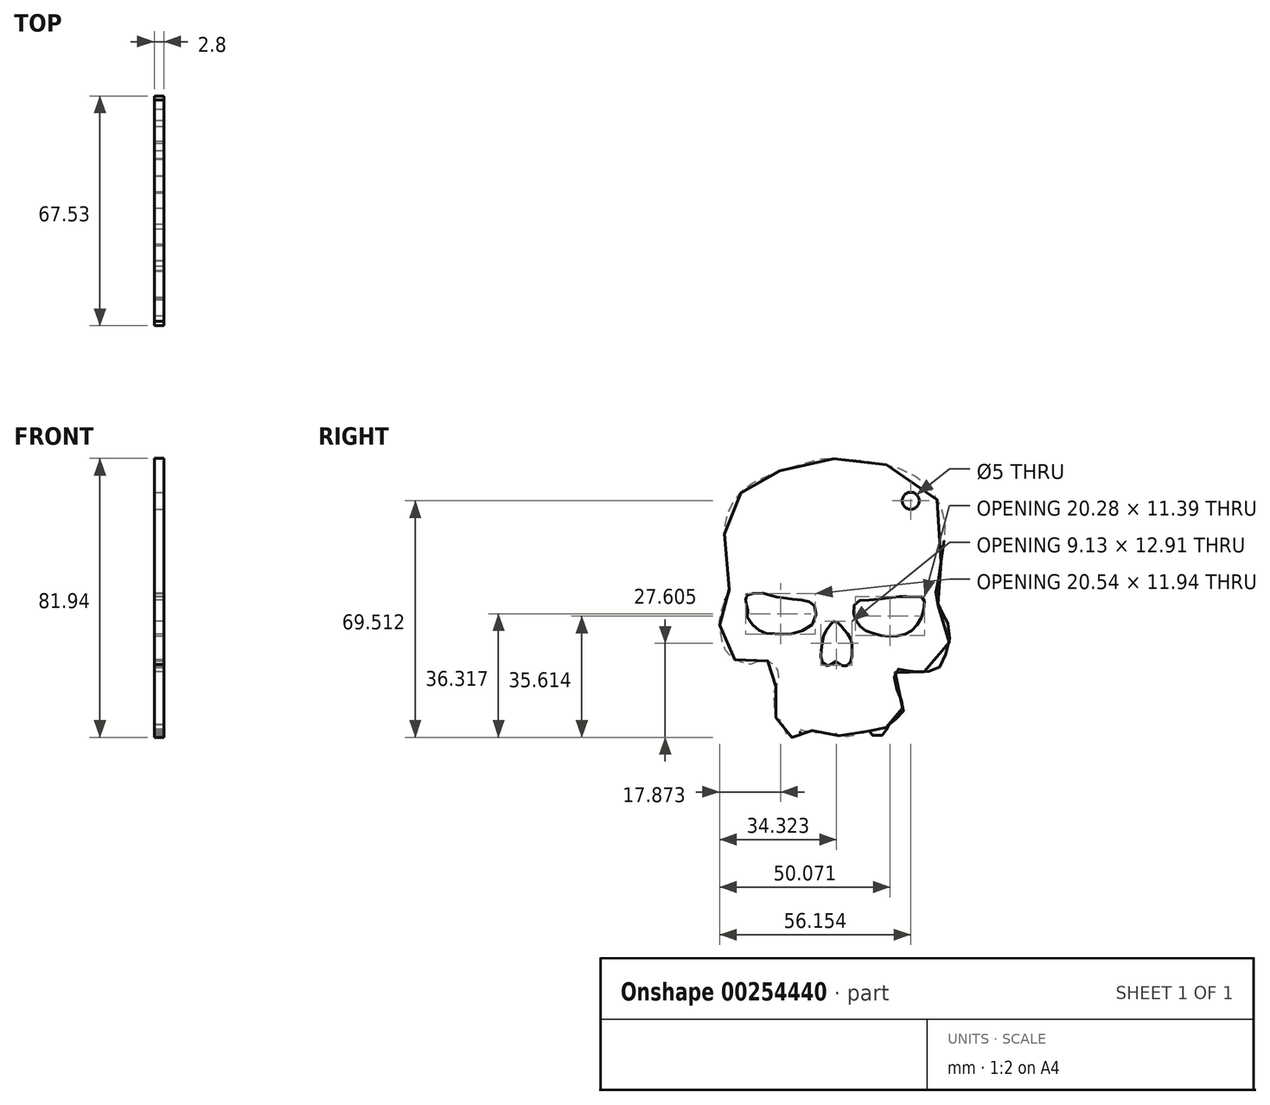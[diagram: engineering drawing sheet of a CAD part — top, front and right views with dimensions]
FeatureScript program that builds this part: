
annotation { "Feature Type Name" : "Feature", "Feature Type Description" : "" }
export const myFeature = defineFeature(function(context is Context, id is Id, definition is map)
    precondition{}
    {
        {
            var Q0;
            Q0=qCreatedBy(makeId("Right.planeOp"),FACE);
            var sketch = newSketch(context, id + "F0", { "sketchPlane" : qUnion([Q0])});
            skFitSpline(sketch, "E0", {"points": [v(-31.63, 2.26) * mm, v(-31.99, 7.13) * mm, v(-32.58, 12.71) * mm, v(-33.06, 19.72) * mm, v(-31.99, 24.46) * mm, v(-31.4, 26.48) * mm, v(-29.02, 29.57) * mm, v(-26.64, 32.3) * mm, v(-23.2, 34.2) * mm, v(-20.35, 35.62) * mm, v(-14.9, 37.64) * mm, v(-8, 39.66) * mm, v(-3.61, 40.61) * mm, v(1.73, 40.37) * mm, v(5.89, 40.25) * mm, v(11.82, 39.3) * mm, v(18.11, 37.76) * mm, v(25.12, 33.96) * mm, v(29.99, 27.55) * mm, v(31.89, 20.43) * mm, v(30.82, 12.47) * mm, v(29.87, 5.11) * mm, v(29.04, 2.14) * mm, v(29.27, 0) * mm, v(29.63, -2.13) * mm, v(30.94, -4.86) * mm, v(32.12, -5.93) * mm, v(32.84, -10.08) * mm, v(32.95, -13.65) * mm, v(31.17, -18.87) * mm, v(29.87, -21) * mm, v(27.26, -21.84) * mm, v(24.53, -22.08) * mm, v(21.32, -21.96) * mm, v(19.9, -21.48) * mm, v(18.95, -20.89) * mm, v(17.76, -21.48) * mm, v(16.93, -22.67) * mm, v(17.16, -25.4) * mm, v(17.88, -28.01) * mm, v(18.83, -30.15) * mm, v(19.3, -32.76) * mm, v(19.54, -34.3) * mm, v(16.93, -36.09) * mm, v(16.1, -37.03) * mm, v(14.9, -37.63) * mm, v(14.43, -37.63) * mm, v(14.55, -39.88) * mm, v(14.32, -40.48) * mm, v(12.65, -40.72) * mm, v(10.87, -40.83) * mm, v(10.16, -40.6) * mm, v(9.45, -39.88) * mm, v(9.45, -39.4) * mm, v(8.38, -39.88) * mm, v(6.12, -40.12) * mm, v(5.41, -40) * mm, v(4.58, -40.83) * mm, v(0.9, -40.95) * mm, v(0, -40.48) * mm, v(0, -40.24) * mm, v(-1.71, -40.6) * mm, v(-4.8, -40) * mm, v(-6.7, -39.88) * mm, v(-7.17, -39.3) * mm, v(-8.48, -39.53) * mm, v(-10.5, -39.17) * mm, v(-11.1, -39.05) * mm, v(-10.62, -40.36) * mm, v(-11.1, -40.72) * mm, v(-13.23, -41.3) * mm, v(-15, -40.36) * mm, v(-15.48, -38.7) * mm, v(-15.37, -37.15) * mm, v(-16.08, -36.56) * mm, v(-17.62, -35.85) * mm, v(-18.1, -35.14) * mm, v(-18.33, -32.88) * mm, v(-18.33, -31.22) * mm, v(-18.57, -29.2) * mm, v(-18.33, -27.06) * mm, v(-17.38, -25.64) * mm, v(-17.03, -23.62) * mm, v(-17.38, -21.72) * mm, v(-18.22, -20.18) * mm, v(-19.52, -19.23) * mm, v(-21.3, -18.51) * mm, v(-23.08, -18.99) * mm, v(-25.34, -19.82) * mm, v(-27.6, -19.46) * mm, v(-30.33, -18.28) * mm, v(-32.46, -16.14) * mm, v(-33.41, -14) * mm, v(-34, -11.63) * mm, v(-34.48, -7.95) * mm, v(-34.24, -5.57) * mm, v(-33.41, -2.37) * mm, v(-32.34, 0) * mm, v(-31.63, 2.26) * mm]});
            skFitSpline(sketch, "E1", {"points": [v(-26.33, -6.03) * mm, v(-26.25, -3.97) * mm, v(-26.33, -2.7) * mm, v(-26.89, -1.75) * mm, v(-26.8, -0.64) * mm, v(-26.65, 0) * mm, v(-26.1, 0.79) * mm, v(-23.8, 0.87) * mm, v(-20.39, 0.95) * mm, v(-18.88, 0) * mm, v(-17.06, 0) * mm, v(-14.92, -0.56) * mm, v(-11.67, -0.8) * mm, v(-8.9, -1.2) * mm, v(-7.4, -1.9) * mm, v(-6.28, -3.49) * mm, v(-6.84, -7.53) * mm, v(-10.96, -10.3) * mm, v(-14.68, -11.02) * mm, v(-17.22, -10.94) * mm, v(-20.23, -10.78) * mm, v(-22.37, -10.15) * mm, v(-24.5, -8.48) * mm, v(-26.33, -6.03) * mm]});
            skFitSpline(sketch, "E2", {"points": [v(25.73, -1.35) * mm, v(25.41, -4.12) * mm, v(24.46, -6.98) * mm, v(22.64, -9.35) * mm, v(20.66, -10.78) * mm, v(18.2, -11.41) * mm, v(15.43, -11.65) * mm, v(12.34, -11.26) * mm, v(9.8, -10.46) * mm, v(7.58, -9.43) * mm, v(6.32, -7.93) * mm, v(5.13, -6.1) * mm, v(4.89, -3.33) * mm, v(6, -1.35) * mm, v(9.72, -0.95) * mm, v(13.45, -0.56) * mm, v(18.04, 0) * mm, v(20.82, 0) * mm, v(23.27, 0) * mm, v(25.02, 0) * mm, v(25.73, -1.35) * mm]});
            skFitSpline(sketch, "E3", {"points": [v(-1.09, -7.25) * mm, v(-2.21, -8.56) * mm, v(-3.22, -10.04) * mm, v(-4.05, -12.18) * mm, v(-4.53, -14.73) * mm, v(-4.7, -16.87) * mm, v(-4.47, -19.12) * mm, v(-3.1, -20.2) * mm, v(-2.21, -20.2) * mm, v(-0.97, -19.42) * mm, v(0, -18.94) * mm, v(0.46, -19.48) * mm, v(1.4, -20.2) * mm, v(2.42, -20.37) * mm, v(3.43, -19.95) * mm, v(4.38, -18.05) * mm, v(4.44, -16.4) * mm, v(4.44, -14.43) * mm, v(4.32, -13) * mm, v(3.55, -11.46) * mm, v(2.48, -10.16) * mm, v(1.76, -9.27) * mm, v(1, -8.26) * mm, v(0, -7.49) * mm, v(-1.09, -7.25) * mm]});
            skSolve(sketch);
        }
        {
            var Q0;
            Q0 = qSketchRegion(id + "F0", true);
            extrude(context, id + "F1", {"entities" : qUnion([Q0]), "depth" : 2.8 * mm});
        }
        {
            var Q0;
            Q0=makeQuery(id+"F1.opExtrude","CAP_FACE",FACE,{"disambiguationData":[OSD([sQuery(id+"F0.wireOp",EDGE,"E0"),sQuery(id+"F0.wireOp",EDGE,"E1"),sQuery(id+"F0.wireOp",EDGE,"E2"),sQuery(id+"F0.wireOp",EDGE,"E3")])],"isStart":false});
            var sketch = newSketch(context, id + "F2", { "sketchPlane" : qUnion([Q0])});
            skPoint(sketch, "E4", {"position": v(21.67, 28.2) * mm});
            skSolve(sketch);
        }
        {
            var Q0;
            Q0=sQuery(id+"F2.wireOp",VERTEX,"E4");
            var Q1;
            Q1=makeQuery(id+"F1.opExtrude","SWEPT_BODY",BODY,{"disambiguationData":[OSD([sQuery(id+"F0.wireOp",EDGE,"E0"),sQuery(id+"F0.wireOp",EDGE,"E1"),sQuery(id+"F0.wireOp",EDGE,"E2"),sQuery(id+"F0.wireOp",EDGE,"E3")])]});
            hole(context, id + "F3", {"style" : HoleStyle.SIMPLE, "endStyle" : HoleEndStyle.BLIND, "holeDiameter" : 5 * mm, "holeDepth" : 12 * mm, "tappedDepth" : 12 * mm, "tapClearance" : 3, "locations" : qUnion([Q0]), "scope" : qUnion([Q1])});
        }
    });
